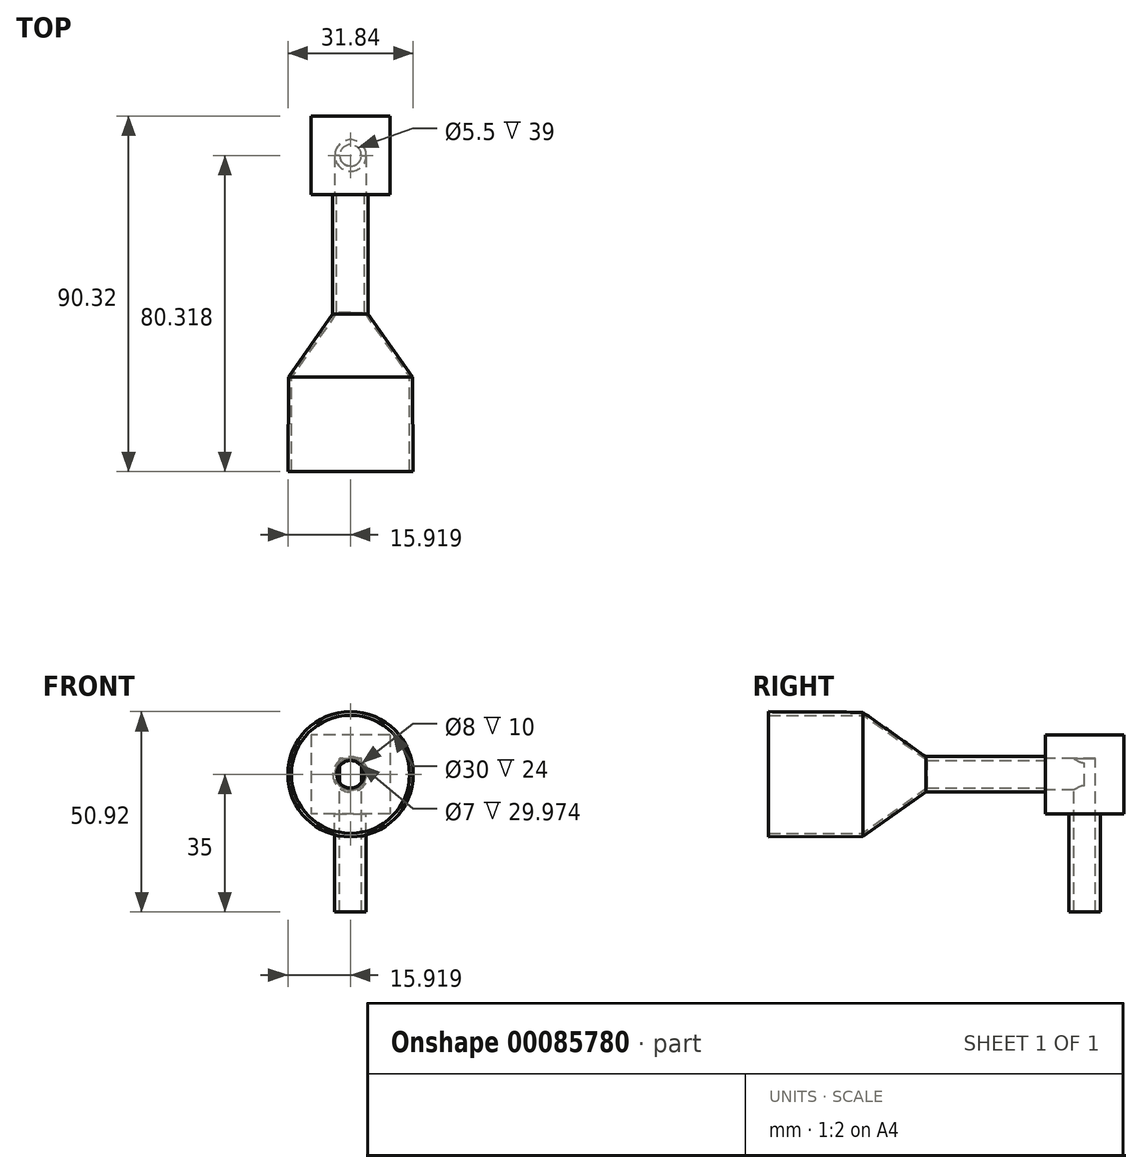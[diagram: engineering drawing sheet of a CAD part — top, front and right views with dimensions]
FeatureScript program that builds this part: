
annotation { "Feature Type Name" : "Feature", "Feature Type Description" : "" }
export const myFeature = defineFeature(function(context is Context, id is Id, definition is map)
    precondition{}
    {
        {
            var Q0;
            Q0=qCreatedBy(makeId("Top.planeOp"),FACE);
            var sketch = newSketch(context, id + "F0", { "sketchPlane" : qUnion([Q0])});
            skLineSegment(sketch, "E0.bottom", {"start": v(-48.56, 36.82) * mm, "end": v(-44.06, 36.82) * mm});
            skLineSegment(sketch, "E0.left", {"start": v(-48.56, 36.82) * mm, "end": v(-48.56, 6.5) * mm});
            skLineSegment(sketch, "E0.right", {"start": v(-44.06, 36.82) * mm, "end": v(-44.06, 11.82) * mm});
            skLineSegment(sketch, "E1", {"start": v(-48.56, 6.5) * mm, "end": v(-59.82, -9.5) * mm});
            skLineSegment(sketch, "E2", {"start": v(-44.06, 11.82) * mm, "end": v(-59.06, -9.5) * mm});
            skLineSegment(sketch, "E3", {"start": v(-59.06, -9.5) * mm, "end": v(-59.06, -33.5) * mm});
            skLineSegment(sketch, "E4", {"start": v(-59.06, -33.5) * mm, "end": v(-59.98, -33.5) * mm});
            skLineSegment(sketch, "E5", {"start": v(-59.98, -33.5) * mm, "end": v(-59.82, -9.5) * mm});
            skLineSegment(sketch, "E6", {"start": v(-59.06, -33.5) * mm, "end": v(-44.06, -33.5) * mm});
            skSolve(sketch);
        }
        {
            var Q0;
            Q0=makeQuery(id+"F0.imprint","IMPRINT",FACE,{"disambiguationData":[TD([[makeQuery(id+"F0.imprint","IMPRINT",EDGE,{"derivedFrom":sQuery(id+"F0.wireOp",EDGE,"E0.bottom")}),-1.0]])]});
            var Q1;
            Q1=sQuery(id+"F0.wireOp",EDGE,"E0.right");
            revolve(context, id + "F1", {"entities" : qUnion([Q0]), "axis" : qUnion([Q1]), "revolveType" : RevolveType.FULL});
        }
        {
            var Q0;
            Q0=makeQuery(id+"F1.opRevolve","SWEPT_FACE",FACE,{"disambiguationData":[OSD([sQuery(id+"F0.wireOp",EDGE,"E0.bottom")])]});
            var sketch = newSketch(context, id + "F2", { "sketchPlane" : qUnion([Q0])});
            skCircle(sketch, "E7", {"center": v(44.06, 0) * mm, "radius": 3.5 * mm});
            skSolve(sketch);
        }
        {
            var Q0;
            Q0 = qSketchRegion(id + "F2", true);
            extrude(context, id + "F3", {"entities" : qUnion([Q0]), "operationType" : NewBodyOperationType.REMOVE, "oppositeDirection" : true, "depth" : 50 * mm});
        }
        {
            var Q0;
            Q0=makeQuery(id+"F1.opRevolve","SWEPT_FACE",FACE,{"disambiguationData":[OSD([sQuery(id+"F0.wireOp",EDGE,"E0.bottom")])]});
            var sketch = newSketch(context, id + "F4", { "sketchPlane" : qUnion([Q0])});
            skLineSegment(sketch, "E8.bottom", {"start": v(34.06, 10) * mm, "end": v(54.06, 10) * mm});
            skLineSegment(sketch, "E8.top", {"start": v(34.06, -10) * mm, "end": v(54.06, -10) * mm});
            skLineSegment(sketch, "E8.left", {"start": v(34.06, 10) * mm, "end": v(34.06, -10) * mm});
            skLineSegment(sketch, "E8.right", {"start": v(54.06, 10) * mm, "end": v(54.06, -10) * mm});
            skPoint(sketch, "E8.middle", {"position": v(44.06, 0) * mm});
            skSolve(sketch);
        }
        {
            var Q0;
            Q0 = qSketchRegion(id + "F4", true);
            extrude(context, id + "F5", {"entities" : qUnion([Q0]), "operationType" : NewBodyOperationType.ADD, "depth" : 20 * mm});
        }
        {
            var Q0;
            {var subQ0=sQuery(id+"F4.wireOp",EDGE,"E8.top");var subQ1=sQuery(id+"F4.wireOp",EDGE,"E8.left");var subQ2=sQuery(id+"F4.wireOp",EDGE,"E8.bottom");var subQ3=sQuery(id+"F4.wireOp",EDGE,"E8.right");Q0=makeQuery(id+"F5.boolean.opBoolean","SPLIT",FACE,{"disambiguationData":[TD([makeQuery(id+"F1.opRevolve","SWEPT_FACE",FACE,{"disambiguationData":[OSD([sQuery(id+"F0.wireOp",EDGE,"E0.left")])]})])],"derivedFrom":makeQuery(id+"F5.opExtrude","CAP_FACE",FACE,{"disambiguationData":[OSD([subQ2,subQ0,subQ1,subQ3])],"isStart":true})});}
            var sketch = newSketch(context, id + "F6", { "sketchPlane" : qUnion([Q0])});
            skCircle(sketch, "E9", {"center": v(-44.06, 0) * mm, "radius": 4 * mm});
            skSolve(sketch);
        }
        {
            var Q0;
            Q0 = qSketchRegion(id + "F6", true);
            extrude(context, id + "F7", {"entities" : qUnion([Q0]), "operationType" : NewBodyOperationType.REMOVE, "oppositeDirection" : true, "depth" : 10 * mm});
        }
        {
            var Q0;
            Q0=makeQuery(id+"F5.opExtrude","SWEPT_FACE",FACE,{"disambiguationData":[OSD([sQuery(id+"F4.wireOp",EDGE,"E8.bottom")])]});
            var sketch = newSketch(context, id + "F8", { "sketchPlane" : qUnion([Q0])});
            skPoint(sketch, "E10", {"position": v(-44.06, 46.82) * mm});
            skPoint(sketch, "E10.positionSnap0", {"position": v(-54.06, 46.82) * mm});
            skPoint(sketch, "E10.positionSnap1", {"position": v(-44.06, 36.82) * mm});
            skSolve(sketch);
        }
        {
            var Q0;
            Q0=sQuery(id+"F8.wireOp",VERTEX,"E10");
            var Q1;
            Q1=makeQuery(id+"F7.boolean.opBoolean","SPLIT",BODY,{"disambiguationData":[OD(1.0)],"derivedFrom":makeQuery(id+"F1.opRevolve","SWEPT_BODY",BODY,{"disambiguationData":[OSD([sQuery(id+"F0.wireOp",EDGE,"E0.bottom"),sQuery(id+"F0.wireOp",EDGE,"E0.left"),sQuery(id+"F0.wireOp",EDGE,"E0.right"),sQuery(id+"F0.wireOp",EDGE,"E1"),sQuery(id+"F0.wireOp",EDGE,"E2"),sQuery(id+"F0.wireOp",EDGE,"E3"),sQuery(id+"F0.wireOp",EDGE,"E4"),sQuery(id+"F0.wireOp",EDGE,"E5")])]})});
            hole(context, id + "F9", {"style" : HoleStyle.SIMPLE, "endStyle" : HoleEndStyle.THROUGH, "holeDiameter" : 5.5 * mm, "locations" : qUnion([Q0]), "scope" : qUnion([Q1]), "isTappedThrough" : true});
        }
        {
            var Q0;
            Q0=makeQuery(id+"F5.opExtrude","SWEPT_FACE",FACE,{"disambiguationData":[OSD([sQuery(id+"F4.wireOp",EDGE,"E8.bottom")])]});
            var sketch = newSketch(context, id + "F10", { "sketchPlane" : qUnion([Q0])});
            skCircle(sketch, "E11", {"center": v(-44.06, 46.82) * mm, "radius": 2.75 * mm});
            skPoint(sketch, "E11.first.point", {"position": v(-43.98, 44.07) * mm});
            skPoint(sketch, "E11.second.point", {"position": v(-44.29, 49.56) * mm});
            skPoint(sketch, "E11.third.point", {"position": v(-46.72, 47.53) * mm});
            skSolve(sketch);
        }
        {
            var Q0;
            Q0 = qSketchRegion(id + "F10", true);
            extrude(context, id + "F11", {"entities" : qUnion([Q0]), "operationType" : NewBodyOperationType.ADD, "oppositeDirection" : true, "depth" : 6 * mm});
        }
        {
            var Q0;
            Q0=makeQuery(id+"F5.opExtrude","SWEPT_FACE",FACE,{"disambiguationData":[OSD([sQuery(id+"F4.wireOp",EDGE,"E8.top")])]});
            var sketch = newSketch(context, id + "F12", { "sketchPlane" : qUnion([Q0])});
            skCircle(sketch, "E12", {"center": v(-44.06, -46.82) * mm, "radius": 2.75 * mm});
            skPoint(sketch, "E12.first.point", {"position": v(-44.07, -44.07) * mm});
            skPoint(sketch, "E12.second.point", {"position": v(-44.06, -49.57) * mm});
            skPoint(sketch, "E12.third.point", {"position": v(-45.85, -48.9) * mm});
            skCircle(sketch, "E13", {"center": v(-44.06, -46.82) * mm, "radius": 4 * mm});
            skSolve(sketch);
        }
        {
            var Q0;
            Q0=makeQuery(id+"F12.imprint","IMPRINT",FACE,{"disambiguationData":[TD([[makeQuery(id+"F12.imprint","IMPRINT",EDGE,{"derivedFrom":sQuery(id+"F12.wireOp",EDGE,"E12")}),-1.0]])]});
            extrude(context, id + "F13", {"entities" : qUnion([Q0]), "operationType" : NewBodyOperationType.ADD, "depth" : 25 * mm});
        }
    });
